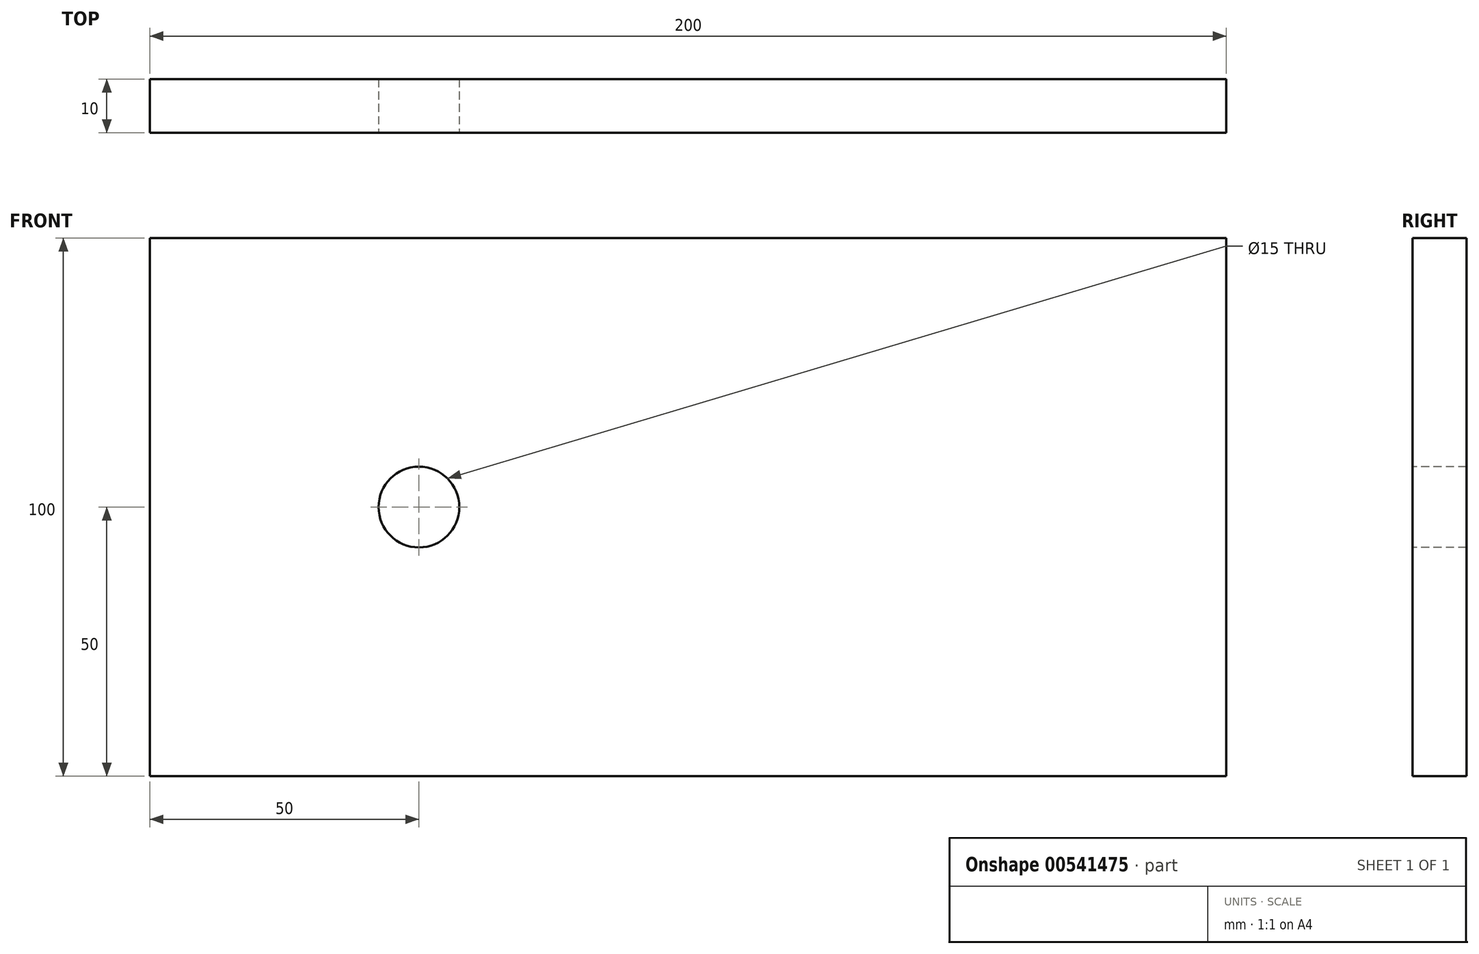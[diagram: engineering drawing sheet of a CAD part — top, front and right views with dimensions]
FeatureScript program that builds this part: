
annotation { "Feature Type Name" : "Feature", "Feature Type Description" : "" }
export const myFeature = defineFeature(function(context is Context, id is Id, definition is map)
    precondition{}
    {
        {
            var Q0;
            Q0=qCreatedBy(makeId("Front.planeOp"),FACE);
            var sketch = newSketch(context, id + "F0", { "sketchPlane" : qUnion([Q0])});
            skLineSegment(sketch, "E0.bottom", {"start": v(-100, 50) * mm, "end": v(100, 50) * mm});
            skLineSegment(sketch, "E0.top", {"start": v(-100, -50) * mm, "end": v(100, -50) * mm});
            skLineSegment(sketch, "E0.left", {"start": v(-100, 50) * mm, "end": v(-100, -50) * mm});
            skLineSegment(sketch, "E0.right", {"start": v(100, 50) * mm, "end": v(100, -50) * mm});
            skPoint(sketch, "E0.middle", {"position": v(0, 0) * mm});
            skCircle(sketch, "E1", {"center": v(-50, 0) * mm, "radius": 7.5 * mm});
            skSolve(sketch);
        }
        {
            var Q0;
            Q0=makeQuery(id+"F0.imprint","IMPRINT",FACE,{"disambiguationData":[TD([[makeQuery(id+"F0.imprint","IMPRINT",EDGE,{"derivedFrom":sQuery(id+"F0.wireOp",EDGE,"E0.bottom")}),-1.0]])]});
            extrude(context, id + "F1", {"entities" : qUnion([Q0]), "oppositeDirection" : true, "depth" : 10 * mm, "offsetDistance" : 25 * mm});
        }
    });
